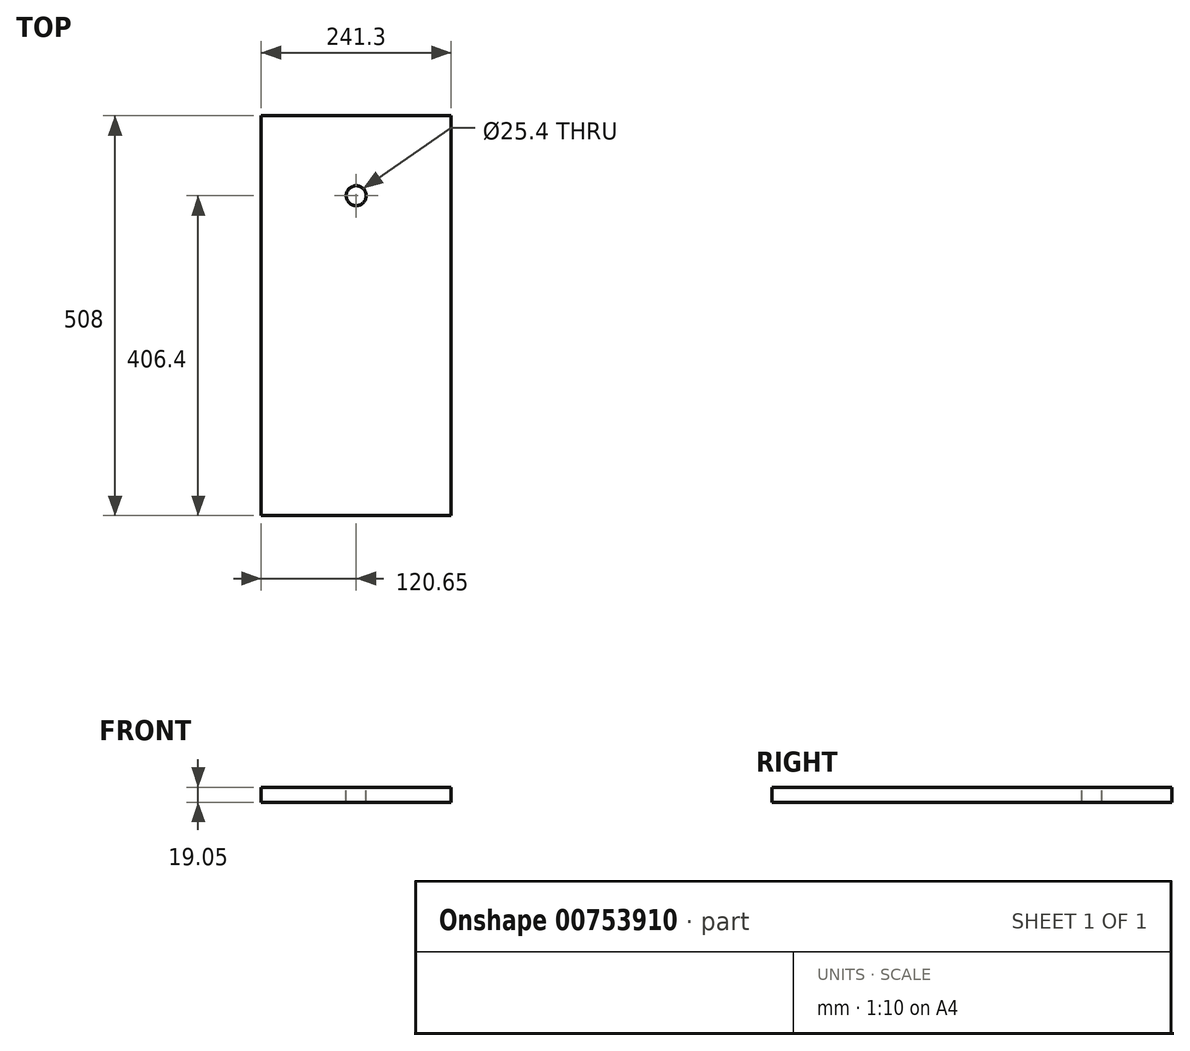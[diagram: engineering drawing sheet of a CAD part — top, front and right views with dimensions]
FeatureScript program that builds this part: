
annotation { "Feature Type Name" : "Feature", "Feature Type Description" : "" }
export const myFeature = defineFeature(function(context is Context, id is Id, definition is map)
    precondition{}
    {
        {
            var Q0;
            Q0=qCreatedBy(makeId("Top.planeOp"),FACE);
            var sketch = newSketch(context, id + "F0", { "sketchPlane" : qUnion([Q0])});
            skLineSegment(sketch, "E0.bottom", {"start": v(120.65, -254) * mm, "end": v(-120.65, -254) * mm});
            skLineSegment(sketch, "E0.top", {"start": v(120.65, 254) * mm, "end": v(-120.65, 254) * mm});
            skLineSegment(sketch, "E0.left", {"start": v(120.65, -254) * mm, "end": v(120.65, 254) * mm});
            skLineSegment(sketch, "E0.right", {"start": v(-120.65, -254) * mm, "end": v(-120.65, 254) * mm});
            skPoint(sketch, "E0.middle", {"position": v(0, 0) * mm});
            skSolve(sketch);
        }
        {
            var Q0;
            Q0=makeQuery(id+"F0.imprint","IMPRINT",FACE,{"disambiguationData":[TD([[makeQuery(id+"F0.imprint","IMPRINT",EDGE,{"derivedFrom":sQuery(id+"F0.wireOp",EDGE,"E0.bottom")}),-1.0]])]});
            extrude(context, id + "F1", {"entities" : qUnion([Q0]), "depth" : 19.05 * mm, "offsetDistance" : 25.4 * mm});
        }
        {
            var Q0;
            Q0=makeQuery(id+"F1.opExtrude","CAP_FACE",FACE,{"disambiguationData":[OSD([sQuery(id+"F0.wireOp",EDGE,"E0.bottom"),sQuery(id+"F0.wireOp",EDGE,"E0.top"),sQuery(id+"F0.wireOp",EDGE,"E0.left"),sQuery(id+"F0.wireOp",EDGE,"E0.right")])],"isStart":false});
            var sketch = newSketch(context, id + "F2", { "sketchPlane" : qUnion([Q0])});
            skLineSegment(sketch, "E1", {"start": v(0, 254) * mm, "end": v(0, 152.4) * mm});
            skCircle(sketch, "E2", {"center": v(0, 152.4) * mm, "radius": 12.7 * mm});
            skSolve(sketch);
        }
        {
            var Q0;
            Q0=makeQuery(id+"F2.imprint","IMPRINT",FACE,{"disambiguationData":[TD([[makeQuery(id+"F2.imprint","IMPRINT",EDGE,{"derivedFrom":sQuery(id+"F2.wireOp",EDGE,"E2")}),1.0]])]});
            extrude(context, id + "F3", {"entities" : qUnion([Q0]), "operationType" : NewBodyOperationType.REMOVE, "endBound" : BoundingType.THROUGH_ALL, "oppositeDirection" : true, "depth" : 25.4 * mm, "offsetDistance" : 25.4 * mm});
        }
    });
